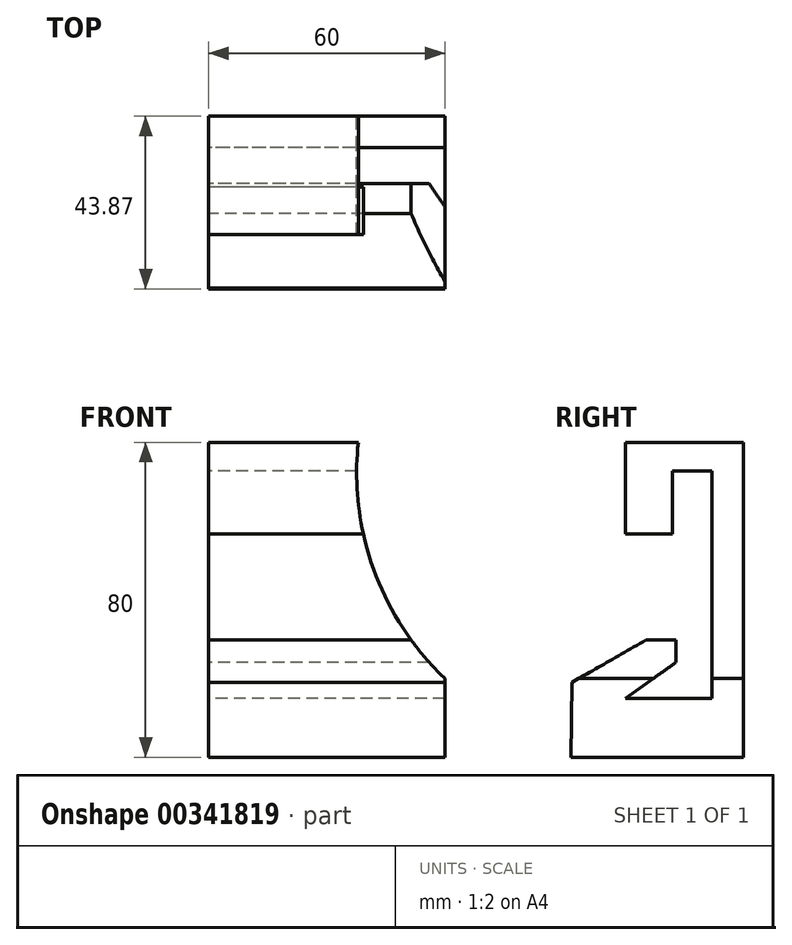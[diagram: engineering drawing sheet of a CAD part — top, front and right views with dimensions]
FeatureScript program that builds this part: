
annotation { "Feature Type Name" : "Feature", "Feature Type Description" : "" }
export const myFeature = defineFeature(function(context is Context, id is Id, definition is map)
    precondition{}
    {
        {
            var Q0;
            Q0=qCreatedBy(makeId("Right.planeOp"),FACE);
            var sketch = newSketch(context, id + "F0", { "sketchPlane" : qUnion([Q0])});
            skLineSegment(sketch, "E0", {"start": v(0, 0) * mm, "end": v(0, 80) * mm});
            skLineSegment(sketch, "E1", {"start": v(-43.87, 0) * mm, "end": v(0, 0) * mm});
            skPoint(sketch, "E2.visualSharp", {"position": v(0.8, 108.98) * mm});
            skLineSegment(sketch, "E3", {"start": v(-43.87, 0) * mm, "end": v(-43.62, 19) * mm});
            skLineSegment(sketch, "E4", {"start": v(0, 80) * mm, "end": v(-30, 80) * mm});
            skLineSegment(sketch, "E5", {"start": v(-30, 80) * mm, "end": v(-30, 56.72) * mm});
            skLineSegment(sketch, "E6", {"start": v(-30, 56.72) * mm, "end": v(-18, 56.72) * mm});
            skLineSegment(sketch, "E7", {"start": v(-18, 56.72) * mm, "end": v(-18, 72.7) * mm});
            skLineSegment(sketch, "E8", {"start": v(-18, 72.7) * mm, "end": v(-8, 72.7) * mm});
            skLineSegment(sketch, "E9", {"start": v(-8, 72.7) * mm, "end": v(-8, 15) * mm});
            skLineSegment(sketch, "E10", {"start": v(-8, 15) * mm, "end": v(-30, 15) * mm});
            skLineSegment(sketch, "E11", {"start": v(-30, 15) * mm, "end": v(-17.12, 24.1) * mm});
            skLineSegment(sketch, "E12", {"start": v(-17.12, 24.1) * mm, "end": v(-17.12, 29.8) * mm});
            skLineSegment(sketch, "E13", {"start": v(-17.12, 29.8) * mm, "end": v(-24.75, 29.8) * mm});
            skLineSegment(sketch, "E14", {"start": v(-24.75, 29.8) * mm, "end": v(-43.62, 19) * mm});
            skSolve(sketch);
        }
        {
            var Q0;
            Q0 = qSketchRegion(id + "F0", true);
            extrude(context, id + "F1", {"entities" : qUnion([Q0]), "depth" : 60 * mm});
        }
        {
            var Q0;
            Q0=makeQuery(id+"F1.opExtrude","SWEPT_FACE",FACE,{"disambiguationData":[OSD([sQuery(id+"F0.wireOp",EDGE,"E0")])]});
            var sketch = newSketch(context, id + "F2", { "sketchPlane" : qUnion([Q0])});
            skArc(sketch, "E15", {"start": v(-60, 20) * mm, "mid": v(-42.02, 47.44) * mm, "end": v(-38, 80) * mm});
            skLineSegment(sketch, "E16.top", {"start": v(-60, 80) * mm, "end": v(-38, 80) * mm});
            skLineSegment(sketch, "E16.left", {"start": v(-60, 20) * mm, "end": v(-60, 80) * mm});
            skSolve(sketch);
        }
        {
            var Q0;
            Q0=makeQuery(id+"F2.imprint","IMPRINT",FACE,{"disambiguationData":[TD([[makeQuery(id+"F2.imprint","IMPRINT",EDGE,{"derivedFrom":sQuery(id+"F2.wireOp",EDGE,"E15")}),1.0]])]});
            extrude(context, id + "F3", {"entities" : qUnion([Q0]), "operationType" : NewBodyOperationType.REMOVE, "endBound" : BoundingType.THROUGH_ALL, "oppositeDirection" : true, "depth" : 25 * mm});
        }
        {
            var Q0;
            Q0=qCreatedBy(makeId("Right.planeOp"),FACE);
            cPlane(context, id + "F4", {"entities" : qUnion([Q0]), "cplaneType" : CPlaneType.OFFSET, "offset" : 30 * mm, "width" : 150 * mm, "height" : 150 * mm});
        }
    });
